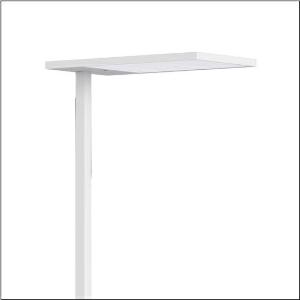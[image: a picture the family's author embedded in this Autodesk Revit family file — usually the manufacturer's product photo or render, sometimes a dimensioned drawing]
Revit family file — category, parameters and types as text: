
# Revit family: silica_21_floor_r_51mx53sg4dw
name_source: partatom
category: Lighting Fixtures
units: mm (PartAtom-declared; Revit-internal decimal feet)

## family parameters
Cut with Voids When Loaded = No
Host = Face
Light Source = No
Part Type = Normal
Room Calculation Point = No
Round Connector Dimension = Use Diameter
Shared = No

## types (1)
- Silica 21 Floor R (1 x LED, 15000 lm, 106.4 W, 4000K)
    Apparent Load = 106 VA
    CIE Flux Codes = 54 86 97 13 100
    Color Rendering = 80
    Color Temperature = 4000K
    Default Elevation = 1800 mm
    Description = Silica® 21 Floor R, floorstanding luminaire, of PMMA, primary optical cover: prismatic diffuser, of PMMA, CAT 2 (L<= 3000cd/m²), light emission: indirect/direct distribution, primary light characteristic: symmetric, primary optical cover: cover panel, of PMMA, installation type: not mounted, LED, rated luminous flux: 15.000lm, luminous efficacy: 141lm/W, light colour: 840, colour temperature: 4000K, control gear: DALI 2, daylight-dependent control, mains connection: 230V, AC, 50/60Hz, connection cable included, cable length: 2,5m, rated input power: 106.4W, luminaire head, of aluminium, powder-coated, traffic white (RAL 9016), length: 671mm, width: 371mm, height: 2010mm, supporting column, angular, of aluminium, powder-coated, traffic white (RAL 9016), baseplate, of steel, powder-coated, traffic white (RAL 9016), sensor module PR3-S, local control - self-sufficient standalone sensors, equipment: master, dimmable, protection rating (complete): IP20, insulation class (complete): insulation class I (protective earthing), certification: CE, permissible operating ambient temperature: 0..+35°C, standard: EN 50419, packaging unit: 1 piece
    Height = 18 mm
    Lamp = 1 x LED
    Lamp Light Flux = 15000 lm
    Lamp Power = 106.4 W
    Lamp count = 1
    Length = 650 mm
    Luminous efficacy = 141 lm/W
    Manufacturer = Siteco
    ModVariant = No
    Model = 51MX53SG4DW
    Mounting Place = Floor
    Mounting Type = Freestanding
    Number of Poles = 1
    OnlyDefault = Yes
    Power Factor = 1
    Product Name = Silica 21 Floor R
    Product group = floorstanding luminaire
    ProductGroupID = 1302
    Protection Class = Protection class I
    Protection Degree = IP 20
    RLX_Detail_Level = 1
    RLX_Emergency_Light_Flux = 0 lm
    RLX_Emergency_Type = 0
    RLX_Emergency_Type_DB = No
    RlxData = <blob elided: 18833 chars, md5=76793188>
    Socket = socket
    Standby Power = 0 W
    System Light Flux = 15000 lm
    System Power = 106 W
    Type Comments = Product without accessories
    Type Image = l_1003935.jpg
    URL = http://relux.com
    VarID = ---
    Voltage = 0 V
    Weight = 0.00 kg
    Width = 350 mm

## geometry (parser evidence)
native form markers: Blend x4, Sweep x16
no freeform markers — native parametric forms only
